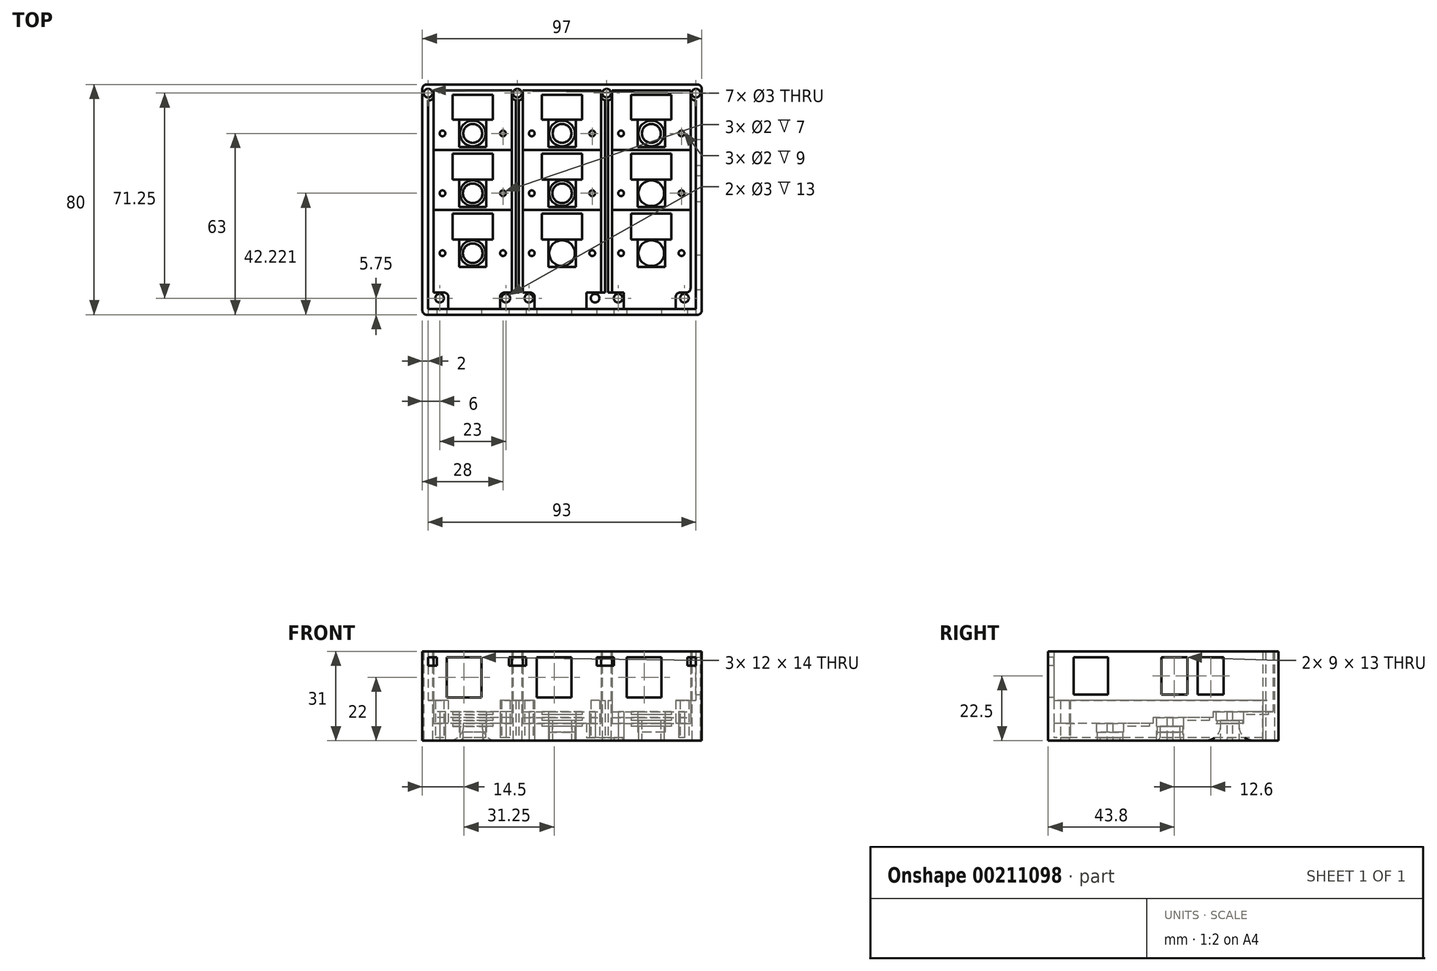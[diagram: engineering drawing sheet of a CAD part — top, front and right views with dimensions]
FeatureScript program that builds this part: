
annotation { "Feature Type Name" : "Feature", "Feature Type Description" : "" }
export const myFeature = defineFeature(function(context is Context, id is Id, definition is map)
    precondition{}
    {
        {
            var Q0;
            Q0=qCreatedBy(makeId("Top.planeOp"),FACE);
            var sketch = newSketch(context, id + "F0", { "sketchPlane" : qUnion([Q0])});
            skLineSegment(sketch, "E0.bottom", {"start": v(33, -40) * mm, "end": v(-33, -40) * mm});
            skLineSegment(sketch, "E0.top", {"start": v(33, 40) * mm, "end": v(-33, 40) * mm});
            skLineSegment(sketch, "E0.right", {"start": v(-33, -40) * mm, "end": v(-33, 40) * mm});
            skPoint(sketch, "E0.middle", {"position": v(0, 0) * mm});
            skLineSegment(sketch, "E1.bottom", {"start": v(31, -38) * mm, "end": v(-31, -38) * mm});
            skLineSegment(sketch, "E1.top", {"start": v(31, 38) * mm, "end": v(-31, 38) * mm});
            skLineSegment(sketch, "E1.right", {"start": v(-31, -38) * mm, "end": v(-31, 38) * mm});
            skLineSegment(sketch, "E2.bottom", {"start": v(-31, 38) * mm, "end": v(-28, 38) * mm});
            skLineSegment(sketch, "E2.left", {"start": v(-31, 38) * mm, "end": v(-31, 34.5) * mm});
            skLineSegment(sketch, "E3.bottom", {"start": v(-1.88, 38) * mm, "end": v(1.88, 38) * mm});
            skLineSegment(sketch, "E3.top", {"start": v(-1.88, 34.5) * mm, "end": v(1.88, 34.5) * mm});
            skLineSegment(sketch, "E3.left", {"start": v(-1.88, 38) * mm, "end": v(-1.88, 34.5) * mm});
            skLineSegment(sketch, "E3.right", {"start": v(1.88, 38) * mm, "end": v(1.88, 34.5) * mm});
            skLineSegment(sketch, "E4.MirrorCS", {"start": v(31, 38) * mm, "end": v(28, 38) * mm});
            skLineSegment(sketch, "E5", {"start": v(-31, -32.3) * mm, "end": v(33, -32.3) * mm});
            skCircle(sketch, "E6", {"center": v(-27, -34.25) * mm, "radius": 1.5 * mm});
            skCircle(sketch, "E7", {"center": v(-4, -34.25) * mm, "radius": 1.5 * mm});
            skCircle(sketch, "E8.MirrorC", {"center": v(4, -34.25) * mm, "radius": 1.5 * mm});
            skCircle(sketch, "E9.MirrorC", {"center": v(27, -34.25) * mm, "radius": 1.5 * mm});
            skLineSegment(sketch, "E10", {"start": v(-1.88, 34.5) * mm, "end": v(-1.88, -32.3) * mm});
            skLineSegment(sketch, "E11.MirrorCS", {"start": v(1.88, 34.5) * mm, "end": v(1.88, -32.3) * mm});
            skPoint(sketch, "E12.centerSnap0", {"position": v(0, 34.5) * mm});
            skCircle(sketch, "E13", {"center": v(-15.5, 23) * mm, "radius": 4.45 * mm});
            skCircle(sketch, "E14", {"center": v(-15.5, 23) * mm, "radius": 3.28 * mm});
            skLineSegment(sketch, "E15.bottom", {"start": v(-10.75, 18.25) * mm, "end": v(-20.25, 18.25) * mm});
            skLineSegment(sketch, "E15.top", {"start": v(-10.75, 27.75) * mm, "end": v(-20.25, 27.75) * mm});
            skLineSegment(sketch, "E15.left", {"start": v(-10.75, 18.25) * mm, "end": v(-10.75, 27.75) * mm});
            skLineSegment(sketch, "E15.right", {"start": v(-20.25, 18.25) * mm, "end": v(-20.25, 27.75) * mm});
            skLineSegment(sketch, "E16.bottom", {"start": v(-22.5, 36.38) * mm, "end": v(-8.5, 36.38) * mm});
            skLineSegment(sketch, "E16.top", {"start": v(-22.5, 27.75) * mm, "end": v(-8.5, 27.75) * mm});
            skLineSegment(sketch, "E16.left", {"start": v(-22.5, 36.38) * mm, "end": v(-22.5, 27.75) * mm});
            skLineSegment(sketch, "E16.right", {"start": v(-8.5, 36.38) * mm, "end": v(-8.5, 27.75) * mm});
            skCircle(sketch, "E17", {"center": v(-15.5, 2.22) * mm, "radius": 4.45 * mm});
            skCircle(sketch, "E18", {"center": v(-15.5, 2.22) * mm, "radius": 3.4 * mm});
            skLineSegment(sketch, "E19.bottom", {"start": v(-10.75, -2.53) * mm, "end": v(-20.25, -2.53) * mm});
            skLineSegment(sketch, "E19.top", {"start": v(-10.75, 6.97) * mm, "end": v(-20.25, 6.97) * mm});
            skLineSegment(sketch, "E19.left", {"start": v(-10.75, -2.53) * mm, "end": v(-10.75, 6.97) * mm});
            skLineSegment(sketch, "E19.right", {"start": v(-20.25, -2.53) * mm, "end": v(-20.25, 6.97) * mm});
            skLineSegment(sketch, "E20.bottom", {"start": v(-22.5, 15.97) * mm, "end": v(-8.5, 15.97) * mm});
            skLineSegment(sketch, "E20.top", {"start": v(-22.5, 6.97) * mm, "end": v(-8.5, 6.97) * mm});
            skLineSegment(sketch, "E20.left", {"start": v(-22.5, 15.97) * mm, "end": v(-22.5, 6.97) * mm});
            skLineSegment(sketch, "E20.right", {"start": v(-8.5, 15.97) * mm, "end": v(-8.5, 6.97) * mm});
            skCircle(sketch, "E21", {"center": v(-15.5, -18.6) * mm, "radius": 4.45 * mm});
            skCircle(sketch, "E22", {"center": v(-15.5, -18.6) * mm, "radius": 3.4 * mm});
            skLineSegment(sketch, "E23.bottom", {"start": v(-10.75, -23.35) * mm, "end": v(-20.25, -23.35) * mm});
            skLineSegment(sketch, "E23.top", {"start": v(-10.75, -13.85) * mm, "end": v(-20.25, -13.85) * mm});
            skLineSegment(sketch, "E23.left", {"start": v(-10.75, -23.35) * mm, "end": v(-10.75, -13.85) * mm});
            skLineSegment(sketch, "E23.right", {"start": v(-20.25, -23.35) * mm, "end": v(-20.25, -13.85) * mm});
            skLineSegment(sketch, "E24.bottom", {"start": v(-22.5, -4.85) * mm, "end": v(-8.5, -4.85) * mm});
            skLineSegment(sketch, "E24.top", {"start": v(-22.5, -13.85) * mm, "end": v(-8.5, -13.85) * mm});
            skLineSegment(sketch, "E24.left", {"start": v(-22.5, -4.85) * mm, "end": v(-22.5, -13.85) * mm});
            skLineSegment(sketch, "E24.right", {"start": v(-8.5, -4.85) * mm, "end": v(-8.5, -13.85) * mm});
            skLineSegment(sketch, "E25.MirrorCS", {"start": v(8.5, 36.38) * mm, "end": v(8.5, 27.75) * mm});
            skLineSegment(sketch, "E26.MirrorCS", {"start": v(22.5, 36.38) * mm, "end": v(8.5, 36.38) * mm});
            skLineSegment(sketch, "E27.MirrorCS", {"start": v(22.5, 36.38) * mm, "end": v(22.5, 27.75) * mm});
            skLineSegment(sketch, "E28.MirrorCS", {"start": v(22.5, 27.75) * mm, "end": v(8.5, 27.75) * mm});
            skCircle(sketch, "E29.MirrorC", {"center": v(15.5, 23) * mm, "radius": 4.45 * mm});
            skCircle(sketch, "E30.MirrorC", {"center": v(15.5, 23) * mm, "radius": 3.28 * mm});
            skLineSegment(sketch, "E31.MirrorCS", {"start": v(22.5, 15.97) * mm, "end": v(8.5, 15.97) * mm});
            skLineSegment(sketch, "E32.MirrorCS", {"start": v(8.5, 15.97) * mm, "end": v(8.5, 6.97) * mm});
            skLineSegment(sketch, "E33.MirrorCS", {"start": v(10.75, 6.97) * mm, "end": v(20.25, 6.97) * mm});
            skLineSegment(sketch, "E34.MirrorCS", {"start": v(22.5, 6.97) * mm, "end": v(8.5, 6.97) * mm});
            skLineSegment(sketch, "E35.MirrorCS", {"start": v(22.5, 15.97) * mm, "end": v(22.5, 6.97) * mm});
            skCircle(sketch, "E36.MirrorC", {"center": v(15.5, 2.22) * mm, "radius": 3.4 * mm});
            skCircle(sketch, "E37.MirrorC", {"center": v(15.5, 2.22) * mm, "radius": 4.45 * mm});
            skLineSegment(sketch, "E38.MirrorCS", {"start": v(10.75, -2.53) * mm, "end": v(20.25, -2.53) * mm});
            skLineSegment(sketch, "E39.MirrorCS", {"start": v(10.75, -2.53) * mm, "end": v(10.75, 6.97) * mm});
            skLineSegment(sketch, "E40.MirrorCS", {"start": v(20.25, -2.53) * mm, "end": v(20.25, 6.97) * mm});
            skLineSegment(sketch, "E41.MirrorCS", {"start": v(10.75, 18.25) * mm, "end": v(10.75, 27.75) * mm});
            skLineSegment(sketch, "E42.MirrorCS", {"start": v(10.75, 18.25) * mm, "end": v(20.25, 18.25) * mm});
            skLineSegment(sketch, "E43.MirrorCS", {"start": v(20.25, 18.25) * mm, "end": v(20.25, 27.75) * mm});
            skLineSegment(sketch, "E44.MirrorCS", {"start": v(22.5, -4.85) * mm, "end": v(8.5, -4.85) * mm});
            skLineSegment(sketch, "E45.MirrorCS", {"start": v(8.5, -4.85) * mm, "end": v(8.5, -13.85) * mm});
            skLineSegment(sketch, "E46.MirrorCS", {"start": v(22.5, -4.85) * mm, "end": v(22.5, -13.85) * mm});
            skLineSegment(sketch, "E47.MirrorCS", {"start": v(10.75, -13.85) * mm, "end": v(20.25, -13.85) * mm});
            skLineSegment(sketch, "E48.MirrorCS", {"start": v(22.5, -13.85) * mm, "end": v(8.5, -13.85) * mm});
            skLineSegment(sketch, "E49.MirrorCS", {"start": v(20.25, -23.35) * mm, "end": v(20.25, -13.85) * mm});
            skCircle(sketch, "E50.MirrorC", {"center": v(15.5, -18.6) * mm, "radius": 4.45 * mm});
            skCircle(sketch, "E51.MirrorC", {"center": v(15.5, -18.6) * mm, "radius": 3.4 * mm});
            skLineSegment(sketch, "E52.MirrorCS", {"start": v(10.75, -23.35) * mm, "end": v(20.25, -23.35) * mm});
            skLineSegment(sketch, "E53.MirrorCS", {"start": v(10.75, -23.35) * mm, "end": v(10.75, -13.85) * mm});
            skLineSegment(sketch, "E54.bottom", {"start": v(-0.5, 34.5) * mm, "end": v(0.5, 34.5) * mm});
            skLineSegment(sketch, "E54.top", {"start": v(-0.5, -32.3) * mm, "end": v(0.5, -32.3) * mm});
            skLineSegment(sketch, "E54.left", {"start": v(-0.5, 34.5) * mm, "end": v(-0.5, -32.3) * mm});
            skLineSegment(sketch, "E54.right", {"start": v(0.5, 34.5) * mm, "end": v(0.5, -32.3) * mm});
            skCircle(sketch, "E55", {"center": v(-31, 37) * mm, "radius": 1.5 * mm});
            skCircle(sketch, "E56", {"center": v(0, 37) * mm, "radius": 1.5 * mm});
            skLineSegment(sketch, "E57", {"start": v(-24, -32.3) * mm, "end": v(-24, -38) * mm});
            skLineSegment(sketch, "E58", {"start": v(-6, -32.3) * mm, "end": v(-6, -38) * mm});
            skLineSegment(sketch, "E59.MirrorCS", {"start": v(6, -32.3) * mm, "end": v(6, -38) * mm});
            skLineSegment(sketch, "E60.MirrorCS", {"start": v(24, -32.3) * mm, "end": v(24, -38) * mm});
            skCircle(sketch, "E61", {"center": v(-5, -18.6) * mm, "radius": 1 * mm});
            skCircle(sketch, "E62", {"center": v(-5, 2.22) * mm, "radius": 1 * mm});
            skCircle(sketch, "E63", {"center": v(-5, 23) * mm, "radius": 1 * mm});
            skLineSegment(sketch, "E64", {"start": v(-15.5, 23) * mm, "end": v(-15.5, -18.6) * mm, "construction": true});
            skCircle(sketch, "E65.MirrorC", {"center": v(-26, 23) * mm, "radius": 1 * mm});
            skCircle(sketch, "E66.MirrorC", {"center": v(-26, 2.22) * mm, "radius": 1 * mm});
            skCircle(sketch, "E67.MirrorC", {"center": v(-26, -18.6) * mm, "radius": 1 * mm});
            skCircle(sketch, "E68.MirrorC", {"center": v(5, 23) * mm, "radius": 1 * mm});
            skCircle(sketch, "E69.MirrorC", {"center": v(5, 2.22) * mm, "radius": 1 * mm});
            skCircle(sketch, "E70.MirrorC", {"center": v(5, -18.6) * mm, "radius": 1 * mm});
            skCircle(sketch, "E71.MirrorC", {"center": v(26, -18.6) * mm, "radius": 1 * mm});
            skCircle(sketch, "E72.MirrorC", {"center": v(26, 2.22) * mm, "radius": 1 * mm});
            skCircle(sketch, "E73.MirrorC", {"center": v(26, 23) * mm, "radius": 1 * mm});
            skLineSegment(sketch, "E74", {"start": v(15.5, 23) * mm, "end": v(15.5, -55.98) * mm, "construction": true});
            skCircle(sketch, "E75.MirrorC", {"center": v(46.5, 23) * mm, "radius": 4.45 * mm});
            skCircle(sketch, "E76.MirrorC", {"center": v(46.5, 23) * mm, "radius": 3.28 * mm});
            skLineSegment(sketch, "E77.MirrorCS", {"start": v(41.75, 27.75) * mm, "end": v(51.25, 27.75) * mm});
            skLineSegment(sketch, "E78.MirrorCS", {"start": v(53.5, 36.38) * mm, "end": v(53.5, 27.75) * mm});
            skLineSegment(sketch, "E79.MirrorCS", {"start": v(53.5, 36.38) * mm, "end": v(39.5, 36.38) * mm});
            skLineSegment(sketch, "E80.MirrorCS", {"start": v(39.5, 36.38) * mm, "end": v(39.5, 27.75) * mm});
            skLineSegment(sketch, "E81.MirrorCS", {"start": v(41.75, 18.25) * mm, "end": v(41.75, 27.75) * mm});
            skLineSegment(sketch, "E82.MirrorCS", {"start": v(51.25, 18.25) * mm, "end": v(51.25, 27.75) * mm});
            skLineSegment(sketch, "E83.MirrorCS", {"start": v(53.5, 27.75) * mm, "end": v(39.5, 27.75) * mm});
            skLineSegment(sketch, "E84.MirrorCS", {"start": v(41.75, 18.25) * mm, "end": v(51.25, 18.25) * mm});
            skLineSegment(sketch, "E85.MirrorCS", {"start": v(62, -38) * mm, "end": v(62, 38) * mm});
            skLineSegment(sketch, "E86.MirrorCS", {"start": v(64, -40) * mm, "end": v(64, 40) * mm});
            skLineSegment(sketch, "E87.MirrorCS", {"start": v(62, 38) * mm, "end": v(62, 34.5) * mm});
            skCircle(sketch, "E88.MirrorC", {"center": v(62, 37) * mm, "radius": 1.5 * mm});
            skLineSegment(sketch, "E89.MirrorCS", {"start": v(-2, 40) * mm, "end": v(64, 40) * mm});
            skLineSegment(sketch, "E90.MirrorCS", {"start": v(0, 38) * mm, "end": v(62, 38) * mm});
            skLineSegment(sketch, "E91.MirrorCS", {"start": v(51.25, -2.53) * mm, "end": v(51.25, 6.97) * mm});
            skLineSegment(sketch, "E92.MirrorCS", {"start": v(41.75, -2.53) * mm, "end": v(51.25, -2.53) * mm});
            skCircle(sketch, "E93.MirrorC", {"center": v(46.5, 2.22) * mm, "radius": 4.45 * mm});
            skCircle(sketch, "E94.MirrorC", {"center": v(46.5, 2.22) * mm, "radius": 3.4 * mm});
            skLineSegment(sketch, "E95.MirrorCS", {"start": v(53.5, 6.97) * mm, "end": v(39.5, 6.97) * mm});
            skLineSegment(sketch, "E96.MirrorCS", {"start": v(53.5, 15.97) * mm, "end": v(53.5, 6.97) * mm});
            skLineSegment(sketch, "E97.MirrorCS", {"start": v(53.5, 15.97) * mm, "end": v(39.5, 15.97) * mm});
            skLineSegment(sketch, "E98.MirrorCS", {"start": v(39.5, 15.97) * mm, "end": v(39.5, 6.97) * mm});
            skLineSegment(sketch, "E99.MirrorCS", {"start": v(41.75, -2.53) * mm, "end": v(41.75, 6.97) * mm});
            skLineSegment(sketch, "E100.MirrorCS", {"start": v(53.5, -4.85) * mm, "end": v(53.5, -13.85) * mm});
            skLineSegment(sketch, "E101.MirrorCS", {"start": v(53.5, -4.85) * mm, "end": v(39.5, -4.85) * mm});
            skLineSegment(sketch, "E102.MirrorCS", {"start": v(53.5, -13.85) * mm, "end": v(39.5, -13.85) * mm});
            skLineSegment(sketch, "E103.MirrorCS", {"start": v(51.25, -23.35) * mm, "end": v(51.25, -13.85) * mm});
            skCircle(sketch, "E104.MirrorC", {"center": v(46.5, -18.6) * mm, "radius": 4.45 * mm});
            skCircle(sketch, "E105.MirrorC", {"center": v(46.5, -18.6) * mm, "radius": 3.4 * mm});
            skLineSegment(sketch, "E106.MirrorCS", {"start": v(41.75, -23.35) * mm, "end": v(51.25, -23.35) * mm});
            skLineSegment(sketch, "E107.MirrorCS", {"start": v(41.75, -23.35) * mm, "end": v(41.75, -13.85) * mm});
            skLineSegment(sketch, "E108.MirrorCS", {"start": v(39.5, -4.85) * mm, "end": v(39.5, -13.85) * mm});
            skLineSegment(sketch, "E109.MirrorCS", {"start": v(62, -32.3) * mm, "end": v(-2, -32.3) * mm});
            skCircle(sketch, "E110.MirrorC", {"center": v(35, -34.25) * mm, "radius": 1.5 * mm});
            skLineSegment(sketch, "E111.MirrorCS", {"start": v(37, -32.3) * mm, "end": v(37, -38) * mm});
            skLineSegment(sketch, "E112.MirrorCS", {"start": v(55, -32.3) * mm, "end": v(55, -38) * mm});
            skLineSegment(sketch, "E113.MirrorCS", {"start": v(0, -38) * mm, "end": v(62, -38) * mm});
            skLineSegment(sketch, "E114.MirrorCS", {"start": v(-2, -40) * mm, "end": v(64, -40) * mm});
            skCircle(sketch, "E115.MirrorC", {"center": v(58, -34.25) * mm, "radius": 1.5 * mm});
            skCircle(sketch, "E116.MirrorC", {"center": v(36, -18.6) * mm, "radius": 1 * mm});
            skCircle(sketch, "E117.MirrorC", {"center": v(36, 2.22) * mm, "radius": 1 * mm});
            skCircle(sketch, "E118.MirrorC", {"center": v(57, 2.22) * mm, "radius": 1 * mm});
            skCircle(sketch, "E119.MirrorC", {"center": v(57, -18.6) * mm, "radius": 1 * mm});
            skCircle(sketch, "E120.MirrorC", {"center": v(57, 23) * mm, "radius": 1 * mm});
            skCircle(sketch, "E121.MirrorC", {"center": v(36, 23) * mm, "radius": 1 * mm});
            skLineSegment(sketch, "E122.MirrorCS", {"start": v(29.12, 34.5) * mm, "end": v(29.12, -32.3) * mm});
            skLineSegment(sketch, "E123.MirrorCS", {"start": v(30.5, 34.5) * mm, "end": v(30.5, -32.3) * mm});
            skLineSegment(sketch, "E124.MirrorCS", {"start": v(31.5, 34.5) * mm, "end": v(31.5, -32.3) * mm});
            skLineSegment(sketch, "E125.MirrorCS", {"start": v(32.88, 34.5) * mm, "end": v(32.88, -32.3) * mm});
            skCircle(sketch, "E126.MirrorC", {"center": v(31, 37) * mm, "radius": 1.5 * mm});
            skLineSegment(sketch, "E127.MirrorCS", {"start": v(29.12, 38) * mm, "end": v(29.12, 34.5) * mm});
            skLineSegment(sketch, "E128.MirrorCS", {"start": v(32.88, 38) * mm, "end": v(32.88, 34.5) * mm});
            skLineSegment(sketch, "E129.MirrorCS", {"start": v(32.88, 34.5) * mm, "end": v(29.12, 34.5) * mm});
            skLineSegment(sketch, "E130", {"start": v(-29.12, 34.5) * mm, "end": v(-29.12, -32.3) * mm});
            skLineSegment(sketch, "E131", {"start": v(-1.88, 17.24) * mm, "end": v(-29.12, 17.2) * mm});
            skLineSegment(sketch, "E132", {"start": v(-1.88, -3.6) * mm, "end": v(-29.12, -3.6) * mm});
            skLineSegment(sketch, "E133.MirrorCS", {"start": v(1.88, -3.6) * mm, "end": v(29.12, -3.6) * mm});
            skLineSegment(sketch, "E134.MirrorCS", {"start": v(1.88, 17.24) * mm, "end": v(29.12, 17.2) * mm});
            skLineSegment(sketch, "E135.MirrorCS", {"start": v(60.12, 34.5) * mm, "end": v(60.12, -32.3) * mm});
            skLineSegment(sketch, "E136.MirrorCS", {"start": v(32.87, 17.24) * mm, "end": v(60.12, 17.2) * mm});
            skLineSegment(sketch, "E137.MirrorCS", {"start": v(32.88, -3.6) * mm, "end": v(60.12, -3.6) * mm});
            skLineSegment(sketch, "E138", {"start": v(-29.12, 34.5) * mm, "end": v(-29.12, 38) * mm});
            skLineSegment(sketch, "E139.MirrorCS", {"start": v(60.12, 34.5) * mm, "end": v(60.12, 38) * mm});
            skLineSegment(sketch, "E140", {"start": v(-31, 34.5) * mm, "end": v(-29.12, 34.5) * mm});
            skLineSegment(sketch, "E141.MirrorCS", {"start": v(62, 34.5) * mm, "end": v(60.12, 34.5) * mm});
            skSolve(sketch);
        }
        {
            var Q0;
            Q0=makeQuery(id+"F0.imprint","IMPRINT",FACE,{"disambiguationData":[TD([[makeQuery(id+"F0.imprint","IMPRINT",EDGE,{"derivedFrom":sQuery(id+"F0.wireOp",EDGE,"E21")}),1.0]])]});
            var Q1;
            Q1=makeQuery(id+"F0.imprint","IMPRINT",FACE,{"disambiguationData":[TD([[makeQuery(id+"F0.imprint","IMPRINT",EDGE,{"derivedFrom":sQuery(id+"F0.wireOp",EDGE,"E54.bottom")}),-1.0]])]});
            var Q2;
            Q2=makeQuery(id+"F0.imprint","IMPRINT",FACE,{"disambiguationData":[TD([[makeQuery(id+"F0.imprint","IMPRINT",EDGE,{"derivedFrom":sQuery(id+"F0.wireOp",EDGE,"E50.MirrorC")}),-1.0]])]});
            var Q3;
            Q3=makeQuery(id+"F0.imprint","IMPRINT",FACE,{"disambiguationData":[TD([[makeQuery(id+"F0.imprint","IMPRINT",EDGE,{"derivedFrom":sQuery(id+"F0.wireOp",EDGE,"E66.MirrorC")}),-1.0]])]});
            var Q4;
            Q4=makeQuery(id+"F0.imprint","IMPRINT",FACE,{"disambiguationData":[TD([[makeQuery(id+"F0.imprint","IMPRINT",EDGE,{"derivedFrom":sQuery(id+"F0.wireOp",EDGE,"E67.MirrorC")}),-1.0]])]});
            var Q5;
            Q5=makeQuery(id+"F0.imprint","IMPRINT",FACE,{"disambiguationData":[TD([[makeQuery(id+"F0.imprint","IMPRINT",EDGE,{"derivedFrom":sQuery(id+"F0.wireOp",EDGE,"E61")}),1.0]])]});
            var Q6;
            Q6=makeQuery(id+"F0.imprint","IMPRINT",FACE,{"disambiguationData":[TD([[makeQuery(id+"F0.imprint","IMPRINT",EDGE,{"derivedFrom":sQuery(id+"F0.wireOp",EDGE,"E62")}),1.0]])]});
            var Q7;
            Q7=makeQuery(id+"F0.imprint","IMPRINT",FACE,{"disambiguationData":[TD([[makeQuery(id+"F0.imprint","IMPRINT",EDGE,{"derivedFrom":sQuery(id+"F0.wireOp",EDGE,"E69.MirrorC")}),-1.0]])]});
            var Q8;
            Q8=makeQuery(id+"F0.imprint","IMPRINT",FACE,{"disambiguationData":[TD([[makeQuery(id+"F0.imprint","IMPRINT",EDGE,{"derivedFrom":sQuery(id+"F0.wireOp",EDGE,"E70.MirrorC")}),-1.0]])]});
            var Q9;
            Q9=makeQuery(id+"F0.imprint","IMPRINT",FACE,{"disambiguationData":[TD([[makeQuery(id+"F0.imprint","IMPRINT",EDGE,{"derivedFrom":sQuery(id+"F0.wireOp",EDGE,"E71.MirrorC")}),1.0]])]});
            var Q10;
            Q10=makeQuery(id+"F0.imprint","IMPRINT",FACE,{"disambiguationData":[TD([[makeQuery(id+"F0.imprint","IMPRINT",EDGE,{"derivedFrom":sQuery(id+"F0.wireOp",EDGE,"E72.MirrorC")}),1.0]])]});
            var Q11;
            Q11=makeQuery(id+"F0.imprint","IMPRINT",FACE,{"disambiguationData":[TD([[makeQuery(id+"F0.imprint","IMPRINT",EDGE,{"derivedFrom":sQuery(id+"F0.wireOp",EDGE,"E7")}),1.0]])]});
            var Q12;
            Q12=makeQuery(id+"F0.imprint","IMPRINT",FACE,{"disambiguationData":[TD([[makeQuery(id+"F0.imprint","IMPRINT",EDGE,{"derivedFrom":sQuery(id+"F0.wireOp",EDGE,"E6")}),1.0]])]});
            var Q13;
            Q13=makeQuery(id+"F0.imprint","IMPRINT",FACE,{"disambiguationData":[TD([[makeQuery(id+"F0.imprint","IMPRINT",EDGE,{"derivedFrom":sQuery(id+"F0.wireOp",EDGE,"E8.MirrorC")}),-1.0]])]});
            var Q14;
            Q14=makeQuery(id+"F0.imprint","IMPRINT",FACE,{"disambiguationData":[TD([[makeQuery(id+"F0.imprint","IMPRINT",EDGE,{"derivedFrom":sQuery(id+"F0.wireOp",EDGE,"E9.MirrorC")}),-1.0]])]});
            var Q15;
            Q15=makeQuery(id+"F0.imprint","IMPRINT",FACE,{"disambiguationData":[TD([[makeQuery(id+"F0.imprint","IMPRINT",EDGE,{"derivedFrom":sQuery(id+"F0.wireOp",EDGE,"E65.MirrorC")}),-1.0]])]});
            var Q16;
            Q16=makeQuery(id+"F0.imprint","IMPRINT",FACE,{"disambiguationData":[TD([[makeQuery(id+"F0.imprint","IMPRINT",EDGE,{"derivedFrom":sQuery(id+"F0.wireOp",EDGE,"E63")}),1.0]])]});
            var Q17;
            Q17=makeQuery(id+"F0.imprint","IMPRINT",FACE,{"disambiguationData":[TD([[makeQuery(id+"F0.imprint","IMPRINT",EDGE,{"derivedFrom":sQuery(id+"F0.wireOp",EDGE,"E68.MirrorC")}),-1.0]])]});
            var Q18;
            Q18=makeQuery(id+"F0.imprint","IMPRINT",FACE,{"disambiguationData":[TD([[makeQuery(id+"F0.imprint","IMPRINT",EDGE,{"derivedFrom":sQuery(id+"F0.wireOp",EDGE,"E73.MirrorC")}),1.0]])]});
            var Q19;
            {var subQ0=sQuery(id+"F0.wireOp",EDGE,"E2.left");var subQ1=sQuery(id+"F0.wireOp",EDGE,"E2.bottom");var subQ2=makeQuery(id+"F0.imprint","INTERSECT",VERTEX,{"derivedFrom":[subQ1,subQ0]});Q19=makeQuery(id+"F0.imprint","IMPRINT",FACE,{"disambiguationData":[TD([[makeQuery(id+"F0.imprint","IMPRINT",EDGE,{"disambiguationData":[TD([[subQ2,-1.0]])],"derivedFrom":subQ1}),-1.0]])]});}
            var Q20;
            {var subQ0=sQuery(id+"F0.wireOp",EDGE,"E56");var subQ1=sQuery(id+"F0.wireOp",EDGE,"E3.bottom");var subQ2=makeQuery(id+"F0.imprint","INTERSECT",VERTEX,{"disambiguationData":[OD(0.0)],"derivedFrom":[subQ1,subQ0]});Q20=makeQuery(id+"F0.imprint","IMPRINT",FACE,{"disambiguationData":[TD([[makeQuery(id+"F0.imprint","IMPRINT",EDGE,{"disambiguationData":[TD([[subQ2,-1.0]])],"derivedFrom":subQ1}),-1.0]])]});}
            var Q21;
            {var subQ0=sQuery(id+"F0.wireOp",EDGE,"4bbdbd1b-dbbd-4441-a1b6-6a8d8a8a4ed50.MirrorCS");var subQ1=sQuery(id+"F0.wireOp",EDGE,"E4.MirrorCS");var subQ2=makeQuery(id+"F0.imprint","INTERSECT",VERTEX,{"derivedFrom":[subQ1,subQ0]});Q21=makeQuery(id+"F0.imprint","IMPRINT",FACE,{"disambiguationData":[TD([[makeQuery(id+"F0.imprint","IMPRINT",EDGE,{"disambiguationData":[TD([[subQ2,-1.0]])],"derivedFrom":subQ1}),1.0]])]});}
            var Q22;
            {var subQ0=sQuery(id+"F0.wireOp",EDGE,"E56");var subQ1=sQuery(id+"F0.wireOp",EDGE,"E3.bottom");var subQ2=makeQuery(id+"F0.imprint","INTERSECT",VERTEX,{"disambiguationData":[OD(0.0)],"derivedFrom":[subQ1,subQ0]});Q22=makeQuery(id+"F0.imprint","IMPRINT",FACE,{"disambiguationData":[TD([[makeQuery(id+"F0.imprint","IMPRINT",EDGE,{"disambiguationData":[TD([[subQ2,-1.0]])],"derivedFrom":subQ1}),1.0]])]});}
            var Q23;
            {var subQ0=sQuery(id+"F0.wireOp",EDGE,"E2.left");var subQ1=sQuery(id+"F0.wireOp",EDGE,"E2.bottom");var subQ2=makeQuery(id+"F0.imprint","INTERSECT",VERTEX,{"derivedFrom":[subQ1,subQ0]});Q23=makeQuery(id+"F0.imprint","IMPRINT",FACE,{"disambiguationData":[TD([[makeQuery(id+"F0.imprint","IMPRINT",EDGE,{"disambiguationData":[TD([[subQ2,-1.0]])],"derivedFrom":subQ1}),1.0]])]});}
            var Q24;
            {var subQ0=sQuery(id+"F0.wireOp",EDGE,"4bbdbd1b-dbbd-4441-a1b6-6a8d8a8a4ed50.MirrorCS");var subQ1=sQuery(id+"F0.wireOp",EDGE,"E4.MirrorCS");var subQ2=makeQuery(id+"F0.imprint","INTERSECT",VERTEX,{"derivedFrom":[subQ1,subQ0]});Q24=makeQuery(id+"F0.imprint","IMPRINT",FACE,{"disambiguationData":[TD([[makeQuery(id+"F0.imprint","IMPRINT",EDGE,{"disambiguationData":[TD([[subQ2,-1.0]])],"derivedFrom":subQ1}),-1.0]])]});}
            var Q25;
            {var subQ1=sQuery(id+"F0.wireOp",EDGE,"a819e3f4-d4a0-4d81-bf29-772e7b22f40c0.MirrorCS");Q25=makeQuery(id+"F0.imprint","IMPRINT",FACE,{"disambiguationData":[TD([[makeQuery(id+"F0.imprint","IMPRINT",EDGE,{"derivedFrom":subQ1}),1.0]])]});}
            var Q26;
            Q26=makeQuery(id+"F0.imprint","IMPRINT",FACE,{"disambiguationData":[TD([[makeQuery(id+"F0.imprint","IMPRINT",EDGE,{"derivedFrom":sQuery(id+"F0.wireOp",EDGE,"E104.MirrorC")}),-1.0]])]});
            var Q27;
            Q27=makeQuery(id+"F0.imprint","IMPRINT",FACE,{"disambiguationData":[TD([[makeQuery(id+"F0.imprint","IMPRINT",EDGE,{"derivedFrom":sQuery(id+"F0.wireOp",EDGE,"E110.MirrorC")}),-1.0]])]});
            var Q28;
            Q28=makeQuery(id+"F0.imprint","IMPRINT",FACE,{"disambiguationData":[TD([[makeQuery(id+"F0.imprint","IMPRINT",EDGE,{"derivedFrom":sQuery(id+"F0.wireOp",EDGE,"E71.MirrorC")}),1.0]])]});
            var Q29;
            Q29=makeQuery(id+"F0.imprint","IMPRINT",FACE,{"disambiguationData":[TD([[makeQuery(id+"F0.imprint","IMPRINT",EDGE,{"derivedFrom":sQuery(id+"F0.wireOp",EDGE,"E115.MirrorC")}),-1.0]])]});
            var Q30;
            Q30=makeQuery(id+"F0.imprint","IMPRINT",FACE,{"disambiguationData":[TD([[makeQuery(id+"F0.imprint","IMPRINT",EDGE,{"derivedFrom":sQuery(id+"F0.wireOp",EDGE,"E119.MirrorC")}),1.0]])]});
            var Q31;
            Q31=makeQuery(id+"F0.imprint","IMPRINT",FACE,{"disambiguationData":[TD([[makeQuery(id+"F0.imprint","IMPRINT",EDGE,{"derivedFrom":sQuery(id+"F0.wireOp",EDGE,"E116.MirrorC")}),-1.0]])]});
            var Q32;
            Q32=makeQuery(id+"F0.imprint","IMPRINT",FACE,{"disambiguationData":[TD([[makeQuery(id+"F0.imprint","IMPRINT",EDGE,{"derivedFrom":sQuery(id+"F0.wireOp",EDGE,"E72.MirrorC")}),1.0]])]});
            var Q33;
            Q33=makeQuery(id+"F0.imprint","IMPRINT",FACE,{"disambiguationData":[TD([[makeQuery(id+"F0.imprint","IMPRINT",EDGE,{"derivedFrom":sQuery(id+"F0.wireOp",EDGE,"E117.MirrorC")}),-1.0]])]});
            var Q34;
            Q34=makeQuery(id+"F0.imprint","IMPRINT",FACE,{"disambiguationData":[TD([[makeQuery(id+"F0.imprint","IMPRINT",EDGE,{"derivedFrom":sQuery(id+"F0.wireOp",EDGE,"E121.MirrorC")}),-1.0]])]});
            var Q35;
            Q35=makeQuery(id+"F0.imprint","IMPRINT",FACE,{"disambiguationData":[TD([[makeQuery(id+"F0.imprint","IMPRINT",EDGE,{"derivedFrom":sQuery(id+"F0.wireOp",EDGE,"E120.MirrorC")}),1.0]])]});
            var Q36;
            {var subQ0=sQuery(id+"F0.wireOp",EDGE,"E90.MirrorCS");var subQ1=makeQuery(id+"F0.imprint","IMPRINT",VERTEX,{"derivedFrom":subQ0});Q36=makeQuery(id+"F0.imprint","IMPRINT",FACE,{"disambiguationData":[TD([[makeQuery(id+"F0.imprint","IMPRINT",EDGE,{"disambiguationData":[TD([[subQ1,1.0]])],"derivedFrom":subQ0}),-1.0]])]});}
            var Q37;
            {var subQ0=sQuery(id+"F0.wireOp",EDGE,"E90.MirrorCS");var subQ1=sQuery(id+"F0.wireOp",EDGE,"E87.MirrorCS");var subQ2=makeQuery(id+"F0.imprint","INTERSECT",VERTEX,{"derivedFrom":[subQ1,subQ0]});Q37=makeQuery(id+"F0.imprint","IMPRINT",FACE,{"disambiguationData":[TD([[makeQuery(id+"F0.imprint","IMPRINT",EDGE,{"disambiguationData":[TD([[subQ2,-1.0]])],"derivedFrom":subQ1}),-1.0]])]});}
            var Q38;
            {var subQ0=sQuery(id+"F0.wireOp",EDGE,"E90.MirrorCS");var subQ1=makeQuery(id+"F0.imprint","IMPRINT",VERTEX,{"derivedFrom":subQ0});Q38=makeQuery(id+"F0.imprint","IMPRINT",FACE,{"disambiguationData":[TD([[makeQuery(id+"F0.imprint","IMPRINT",EDGE,{"disambiguationData":[TD([[subQ1,1.0]])],"derivedFrom":subQ0}),1.0]])]});}
            var Q39;
            {var subQ0=sQuery(id+"F0.wireOp",EDGE,"E90.MirrorCS");var subQ1=sQuery(id+"F0.wireOp",EDGE,"E87.MirrorCS");var subQ2=makeQuery(id+"F0.imprint","INTERSECT",VERTEX,{"derivedFrom":[subQ1,subQ0]});Q39=makeQuery(id+"F0.imprint","IMPRINT",FACE,{"disambiguationData":[TD([[makeQuery(id+"F0.imprint","IMPRINT",EDGE,{"disambiguationData":[TD([[subQ2,-1.0]])],"derivedFrom":subQ1}),1.0]])]});}
            var Q40;
            Q40=makeQuery(id+"F0.imprint","IMPRINT",FACE,{"disambiguationData":[TD([[makeQuery(id+"F0.imprint","IMPRINT",EDGE,{"derivedFrom":sQuery(id+"F0.wireOp",EDGE,"E118.MirrorC")}),1.0]])]});
            var Q41;
            {var subQ0=sQuery(id+"F0.wireOp",EDGE,"1d7a142f-2401-46ea-bbda-0649d409a4330.MirrorCS");Q41=makeQuery(id+"F0.imprint","IMPRINT",FACE,{"disambiguationData":[TD([[makeQuery(id+"F0.imprint","IMPRINT",EDGE,{"derivedFrom":subQ0}),1.0]])]});}
            var Q42;
            {var subQ0=sQuery(id+"F0.wireOp",EDGE,"E123.MirrorCS");Q42=makeQuery(id+"F0.imprint","IMPRINT",FACE,{"disambiguationData":[TD([[makeQuery(id+"F0.imprint","IMPRINT",EDGE,{"derivedFrom":subQ0}),1.0]])]});}
            extrude(context, id + "F1", {"entities" : qUnion([Q0, Q1, Q2, Q3, Q4, Q5, Q6, Q7, Q8, Q9, Q10, Q11, Q12, Q13, Q14, Q15, Q16, Q17, Q18, Q19, Q20, Q21, Q22, Q23, Q24, Q25, Q26, Q27, Q28, Q29, Q30, Q31, Q32, Q33, Q34, Q35, Q36, Q37, Q38, Q39, Q40, Q41, Q42]), "depth" : 1 * mm});
        }
        {
            var Q0;
            Q0=makeQuery(id+"F0.imprint","IMPRINT",FACE,{"disambiguationData":[TD([[makeQuery(id+"F0.imprint","IMPRINT",EDGE,{"derivedFrom":sQuery(id+"F0.wireOp",EDGE,"E21")}),-1.0]])]});
            var Q1;
            {var subQ0=sQuery(id+"F0.wireOp",EDGE,"E49.MirrorCS");Q1=makeQuery(id+"F0.imprint","IMPRINT",FACE,{"disambiguationData":[TD([[makeQuery(id+"F0.imprint","IMPRINT",EDGE,{"derivedFrom":subQ0}),1.0]])]});}
            var Q2;
            Q2=makeQuery(id+"F0.imprint","IMPRINT",FACE,{"disambiguationData":[TD([[makeQuery(id+"F0.imprint","IMPRINT",EDGE,{"derivedFrom":sQuery(id+"F0.wireOp",EDGE,"E17")}),1.0]])]});
            var Q3;
            Q3=makeQuery(id+"F0.imprint","IMPRINT",FACE,{"disambiguationData":[TD([[makeQuery(id+"F0.imprint","IMPRINT",EDGE,{"derivedFrom":sQuery(id+"F0.wireOp",EDGE,"E36.MirrorC")}),1.0]])]});
            var Q4;
            {var subQ0=sQuery(id+"F0.wireOp",EDGE,"E103.MirrorCS");Q4=makeQuery(id+"F0.imprint","IMPRINT",FACE,{"disambiguationData":[TD([[makeQuery(id+"F0.imprint","IMPRINT",EDGE,{"derivedFrom":subQ0}),1.0]])]});}
            var Q5;
            Q5=makeQuery(id+"F0.imprint","IMPRINT",FACE,{"disambiguationData":[TD([[makeQuery(id+"F0.imprint","IMPRINT",EDGE,{"derivedFrom":sQuery(id+"F0.wireOp",EDGE,"E93.MirrorC")}),-1.0]])]});
            extrude(context, id + "F2", {"entities" : qUnion([Q0, Q1, Q2, Q3, Q4, Q5]), "operationType" : NewBodyOperationType.ADD, "depth" : 3 * mm});
        }
        {
            var Q0;
            Q0=makeQuery(id+"F0.imprint","IMPRINT",FACE,{"disambiguationData":[TD([[makeQuery(id+"F0.imprint","IMPRINT",EDGE,{"derivedFrom":sQuery(id+"F0.wireOp",EDGE,"E20.bottom")}),-1.0]])]});
            var Q1;
            Q1=makeQuery(id+"F0.imprint","IMPRINT",FACE,{"disambiguationData":[TD([[makeQuery(id+"F0.imprint","IMPRINT",EDGE,{"derivedFrom":sQuery(id+"F0.wireOp",EDGE,"E13")}),-1.0]])]});
            var Q2;
            Q2=makeQuery(id+"F0.imprint","IMPRINT",FACE,{"disambiguationData":[TD([[makeQuery(id+"F0.imprint","IMPRINT",EDGE,{"derivedFrom":sQuery(id+"F0.wireOp",EDGE,"E31.MirrorCS")}),1.0]])]});
            var Q3;
            Q3=makeQuery(id+"F0.imprint","IMPRINT",FACE,{"disambiguationData":[TD([[makeQuery(id+"F0.imprint","IMPRINT",EDGE,{"derivedFrom":sQuery(id+"F0.wireOp",EDGE,"E29.MirrorC")}),1.0]])]});
            var Q4;
            {var subQ0=sQuery(id+"F0.wireOp",EDGE,"E96.MirrorCS");Q4=makeQuery(id+"F0.imprint","IMPRINT",FACE,{"disambiguationData":[TD([[makeQuery(id+"F0.imprint","IMPRINT",EDGE,{"derivedFrom":subQ0}),-1.0]])]});}
            var Q5;
            Q5=makeQuery(id+"F0.imprint","IMPRINT",FACE,{"disambiguationData":[TD([[makeQuery(id+"F0.imprint","IMPRINT",EDGE,{"derivedFrom":sQuery(id+"F0.wireOp",EDGE,"E75.MirrorC")}),1.0]])]});
            extrude(context, id + "F3", {"entities" : qUnion([Q0, Q1, Q2, Q3, Q4, Q5]), "operationType" : NewBodyOperationType.ADD, "depth" : 7 * mm});
        }
        {
            var Q0;
            Q0=makeQuery(id+"F0.imprint","IMPRINT",FACE,{"disambiguationData":[TD([[makeQuery(id+"F0.imprint","IMPRINT",EDGE,{"derivedFrom":sQuery(id+"F0.wireOp",EDGE,"E19.bottom")}),1.0]])]});
            var Q1;
            Q1=makeQuery(id+"F0.imprint","IMPRINT",FACE,{"disambiguationData":[TD([[makeQuery(id+"F0.imprint","IMPRINT",EDGE,{"derivedFrom":sQuery(id+"F0.wireOp",EDGE,"E31.MirrorCS")}),-1.0]])]});
            var Q2;
            {var subQ5=sQuery(id+"F0.wireOp",EDGE,"E91.MirrorCS");Q2=makeQuery(id+"F0.imprint","IMPRINT",FACE,{"disambiguationData":[TD([[makeQuery(id+"F0.imprint","IMPRINT",EDGE,{"derivedFrom":subQ5}),-1.0]])]});}
            extrude(context, id + "F4", {"entities" : qUnion([Q0, Q1, Q2]), "operationType" : NewBodyOperationType.ADD, "depth" : 8 * mm});
        }
        {
            var Q0;
            Q0=makeQuery(id+"F0.imprint","IMPRINT",FACE,{"disambiguationData":[TD([[makeQuery(id+"F0.imprint","IMPRINT",EDGE,{"derivedFrom":sQuery(id+"F0.wireOp",EDGE,"E16.bottom")}),-1.0]])]});
            var Q1;
            {var subQ3=sQuery(id+"F0.wireOp",EDGE,"E25.MirrorCS");Q1=makeQuery(id+"F0.imprint","IMPRINT",FACE,{"disambiguationData":[TD([[makeQuery(id+"F0.imprint","IMPRINT",EDGE,{"derivedFrom":subQ3}),1.0]])]});}
            var Q2;
            {var subQ1=sQuery(id+"F0.wireOp",EDGE,"E78.MirrorCS");Q2=makeQuery(id+"F0.imprint","IMPRINT",FACE,{"disambiguationData":[TD([[makeQuery(id+"F0.imprint","IMPRINT",EDGE,{"derivedFrom":subQ1}),-1.0]])]});}
            extrude(context, id + "F5", {"entities" : qUnion([Q0, Q1, Q2]), "operationType" : NewBodyOperationType.ADD, "depth" : 9 * mm});
        }
        {
            var Q0;
            {var subQ4=sQuery(id+"F0.wireOp",EDGE,"E3.left");Q0=makeQuery(id+"F0.imprint","IMPRINT",FACE,{"disambiguationData":[TD([[makeQuery(id+"F0.imprint","IMPRINT",EDGE,{"derivedFrom":subQ4}),-1.0]])]});}
            var Q1;
            {var subQ9=sQuery(id+"F0.wireOp",EDGE,"E3.right");Q1=makeQuery(id+"F0.imprint","IMPRINT",FACE,{"disambiguationData":[TD([[makeQuery(id+"F0.imprint","IMPRINT",EDGE,{"derivedFrom":subQ9}),1.0]])]});}
            var Q2;
            {var subQ5=sQuery(id+"F0.wireOp",EDGE,"0ee36956-4347-4c33-b409-07fdfe6817680.MirrorCS");Q2=makeQuery(id+"F0.imprint","IMPRINT",FACE,{"disambiguationData":[TD([[makeQuery(id+"F0.imprint","IMPRINT",EDGE,{"derivedFrom":subQ5}),-1.0]])]});}
            var Q3;
            {var subQ6=sQuery(id+"F0.wireOp",EDGE,"E78.MirrorCS");Q3=makeQuery(id+"F0.imprint","IMPRINT",FACE,{"disambiguationData":[TD([[makeQuery(id+"F0.imprint","IMPRINT",EDGE,{"derivedFrom":subQ6}),1.0]])]});}
            extrude(context, id + "F6", {"entities" : qUnion([Q0, Q1, Q2, Q3]), "operationType" : NewBodyOperationType.ADD, "depth" : 10 * mm});
        }
        {
            var Q0;
            Q0=makeQuery(id+"F0.imprint","IMPRINT",FACE,{"disambiguationData":[TD([[makeQuery(id+"F0.imprint","IMPRINT",EDGE,{"derivedFrom":sQuery(id+"F0.wireOp",EDGE,"E24.bottom")}),-1.0]])]});
            var Q1;
            Q1=makeQuery(id+"F0.imprint","IMPRINT",FACE,{"disambiguationData":[TD([[makeQuery(id+"F0.imprint","IMPRINT",EDGE,{"derivedFrom":sQuery(id+"F0.wireOp",EDGE,"E44.MirrorCS")}),1.0]])]});
            var Q2;
            Q2=makeQuery(id+"F0.imprint","IMPRINT",FACE,{"disambiguationData":[TD([[makeQuery(id+"F0.imprint","IMPRINT",EDGE,{"derivedFrom":sQuery(id+"F0.wireOp",EDGE,"E17")}),-1.0]])]});
            var Q3;
            Q3=makeQuery(id+"F0.imprint","IMPRINT",FACE,{"disambiguationData":[TD([[makeQuery(id+"F0.imprint","IMPRINT",EDGE,{"derivedFrom":sQuery(id+"F0.wireOp",EDGE,"E37.MirrorC")}),1.0]])]});
            var Q4;
            {var subQ4=sQuery(id+"F0.wireOp",EDGE,"E100.MirrorCS");Q4=makeQuery(id+"F0.imprint","IMPRINT",FACE,{"disambiguationData":[TD([[makeQuery(id+"F0.imprint","IMPRINT",EDGE,{"derivedFrom":subQ4}),-1.0]])]});}
            var Q5;
            {var subQ1=sQuery(id+"F0.wireOp",EDGE,"E91.MirrorCS");Q5=makeQuery(id+"F0.imprint","IMPRINT",FACE,{"disambiguationData":[TD([[makeQuery(id+"F0.imprint","IMPRINT",EDGE,{"derivedFrom":subQ1}),1.0]])]});}
            extrude(context, id + "F7", {"entities" : qUnion([Q0, Q1, Q2, Q3, Q4, Q5]), "operationType" : NewBodyOperationType.ADD, "depth" : 5 * mm});
        }
        {
            var Q0;
            {var subQ10=sQuery(id+"F0.wireOp",EDGE,"as5H9wRG-vlFi-IaeT-bpy4-L7joDgvUDys8");Q0=makeQuery(id+"F0.imprint","IMPRINT",FACE,{"disambiguationData":[TD([[makeQuery(id+"F0.imprint","IMPRINT",EDGE,{"derivedFrom":subQ10}),1.0]])]});}
            var Q1;
            {var subQ10=sQuery(id+"F0.wireOp",EDGE,"efb54391-69b0-4f1c-9c84-c88345ef56250.MirrorCS");Q1=makeQuery(id+"F0.imprint","IMPRINT",FACE,{"disambiguationData":[TD([[makeQuery(id+"F0.imprint","IMPRINT",EDGE,{"derivedFrom":subQ10}),-1.0]])]});}
            var Q2;
            Q2=makeQuery(id+"F0.imprint","IMPRINT",FACE,{"disambiguationData":[TD([[makeQuery(id+"F0.imprint","IMPRINT",EDGE,{"derivedFrom":sQuery(id+"F0.wireOp",EDGE,"E13")}),1.0]])]});
            var Q3;
            Q3=makeQuery(id+"F0.imprint","IMPRINT",FACE,{"disambiguationData":[TD([[makeQuery(id+"F0.imprint","IMPRINT",EDGE,{"derivedFrom":sQuery(id+"F0.wireOp",EDGE,"E29.MirrorC")}),-1.0]])]});
            var Q4;
            {var subQ0=sQuery(id+"F0.wireOp",EDGE,"E57");Q4=makeQuery(id+"F0.imprint","IMPRINT",FACE,{"disambiguationData":[TD([[makeQuery(id+"F0.imprint","IMPRINT",EDGE,{"derivedFrom":subQ0}),1.0]])]});}
            var Q5;
            {var subQ0=sQuery(id+"F0.wireOp",EDGE,"E59.MirrorCS");Q5=makeQuery(id+"F0.imprint","IMPRINT",FACE,{"disambiguationData":[TD([[makeQuery(id+"F0.imprint","IMPRINT",EDGE,{"derivedFrom":subQ0}),1.0]])]});}
            var Q6;
            {var subQ0=sQuery(id+"F0.wireOp",EDGE,"E111.MirrorCS");Q6=makeQuery(id+"F0.imprint","IMPRINT",FACE,{"disambiguationData":[TD([[makeQuery(id+"F0.imprint","IMPRINT",EDGE,{"derivedFrom":subQ0}),1.0]])]});}
            var Q7;
            {var subQ8=sQuery(id+"F0.wireOp",EDGE,"a2697284-5f4f-4e30-b8e9-a0291027fc0e0.MirrorCS");Q7=makeQuery(id+"F0.imprint","IMPRINT",FACE,{"disambiguationData":[TD([[makeQuery(id+"F0.imprint","IMPRINT",EDGE,{"derivedFrom":subQ8}),-1.0]])]});}
            var Q8;
            Q8=makeQuery(id+"F0.imprint","IMPRINT",FACE,{"disambiguationData":[TD([[makeQuery(id+"F0.imprint","IMPRINT",EDGE,{"derivedFrom":sQuery(id+"F0.wireOp",EDGE,"E75.MirrorC")}),-1.0]])]});
            var Q9;
            Q9=makeQuery(id+"F0.imprint","IMPRINT",FACE,{"disambiguationData":[TD([[makeQuery(id+"F0.imprint","IMPRINT",EDGE,{"derivedFrom":sQuery(id+"F0.wireOp",EDGE,"E23.bottom")}),1.0]])]});
            var Q10;
            Q10=makeQuery(id+"F0.imprint","IMPRINT",FACE,{"disambiguationData":[TD([[makeQuery(id+"F0.imprint","IMPRINT",EDGE,{"derivedFrom":sQuery(id+"F0.wireOp",EDGE,"E44.MirrorCS")}),-1.0]])]});
            var Q11;
            {var subQ5=sQuery(id+"F0.wireOp",EDGE,"E100.MirrorCS");Q11=makeQuery(id+"F0.imprint","IMPRINT",FACE,{"disambiguationData":[TD([[makeQuery(id+"F0.imprint","IMPRINT",EDGE,{"derivedFrom":subQ5}),1.0]])]});}
            extrude(context, id + "F8", {"entities" : qUnion([Q0, Q1, Q2, Q3, Q4, Q5, Q6, Q7, Q8, Q9, Q10, Q11]), "operationType" : NewBodyOperationType.ADD, "depth" : 6 * mm});
        }
        {
            var Q0;
            {var subQ7=sQuery(id+"F0.wireOp",EDGE,"E54.left");Q0=makeQuery(id+"F0.imprint","IMPRINT",FACE,{"disambiguationData":[TD([[makeQuery(id+"F0.imprint","IMPRINT",EDGE,{"derivedFrom":subQ7}),-1.0]])]});}
            var Q1;
            {var subQ5=sQuery(id+"F0.wireOp",EDGE,"E54.right");Q1=makeQuery(id+"F0.imprint","IMPRINT",FACE,{"disambiguationData":[TD([[makeQuery(id+"F0.imprint","IMPRINT",EDGE,{"derivedFrom":subQ5}),1.0]])]});}
            var Q2;
            {var subQ5=sQuery(id+"F0.wireOp",EDGE,"E2.top");Q2=makeQuery(id+"F0.imprint","IMPRINT",FACE,{"disambiguationData":[TD([[makeQuery(id+"F0.imprint","IMPRINT",EDGE,{"derivedFrom":subQ5}),-1.0]])]});}
            var Q3;
            {var subQ1=sQuery(id+"F0.wireOp",EDGE,"ab46168d-af6e-42de-824f-0888a4270b770.MirrorCS");Q3=makeQuery(id+"F0.imprint","IMPRINT",FACE,{"disambiguationData":[TD([[makeQuery(id+"F0.imprint","IMPRINT",EDGE,{"derivedFrom":subQ1}),1.0]])]});}
            var Q4;
            Q4=makeQuery(id+"F0.imprint","IMPRINT",FACE,{"disambiguationData":[TD([[makeQuery(id+"F0.imprint","IMPRINT",EDGE,{"derivedFrom":sQuery(id+"F0.wireOp",EDGE,"E6")}),-1.0]])]});
            var Q5;
            Q5=makeQuery(id+"F0.imprint","IMPRINT",FACE,{"disambiguationData":[TD([[makeQuery(id+"F0.imprint","IMPRINT",EDGE,{"derivedFrom":sQuery(id+"F0.wireOp",EDGE,"E7")}),-1.0]])]});
            var Q6;
            Q6=makeQuery(id+"F0.imprint","IMPRINT",FACE,{"disambiguationData":[TD([[makeQuery(id+"F0.imprint","IMPRINT",EDGE,{"derivedFrom":sQuery(id+"F0.wireOp",EDGE,"E9.MirrorC")}),1.0]])]});
            var Q7;
            {var subQ7=sQuery(id+"F0.wireOp",EDGE,"39177a82-2316-4fb4-a93a-6d32d1cb23ba0.MirrorCS");Q7=makeQuery(id+"F0.imprint","IMPRINT",FACE,{"disambiguationData":[TD([[makeQuery(id+"F0.imprint","IMPRINT",EDGE,{"derivedFrom":subQ7}),1.0]])]});}
            var Q8;
            {var subQ0=sQuery(id+"F0.wireOp",EDGE,"a819e3f4-d4a0-4d81-bf29-772e7b22f40c0.MirrorCS");Q8=makeQuery(id+"F0.imprint","IMPRINT",FACE,{"disambiguationData":[TD([[makeQuery(id+"F0.imprint","IMPRINT",EDGE,{"derivedFrom":subQ0}),-1.0]])]});}
            var Q9;
            {var subQ0=sQuery(id+"F0.wireOp",EDGE,"cd15d214-6c87-4102-83e1-9705ae7459630.MirrorCS");Q9=makeQuery(id+"F0.imprint","IMPRINT",FACE,{"disambiguationData":[TD([[makeQuery(id+"F0.imprint","IMPRINT",EDGE,{"derivedFrom":subQ0}),1.0]])]});}
            var Q10;
            {var subQ0=sQuery(id+"F0.wireOp",EDGE,"E112.MirrorCS");Q10=makeQuery(id+"F0.imprint","IMPRINT",FACE,{"disambiguationData":[TD([[makeQuery(id+"F0.imprint","IMPRINT",EDGE,{"derivedFrom":subQ0}),1.0]])]});}
            var Q11;
            {var subQ3=sQuery(id+"F0.wireOp",EDGE,"b6e59eed-b5e8-4de3-8956-2fd325e44a850.MirrorCS");Q11=makeQuery(id+"F0.imprint","IMPRINT",FACE,{"disambiguationData":[TD([[makeQuery(id+"F0.imprint","IMPRINT",EDGE,{"derivedFrom":subQ3}),1.0]])]});}
            var Q12;
            {var subQ7=sQuery(id+"F0.wireOp",EDGE,"E123.MirrorCS");Q12=makeQuery(id+"F0.imprint","IMPRINT",FACE,{"disambiguationData":[TD([[makeQuery(id+"F0.imprint","IMPRINT",EDGE,{"derivedFrom":subQ7}),-1.0]])]});}
            var Q13;
            {var subQ5=sQuery(id+"F0.wireOp",EDGE,"E124.MirrorCS");Q13=makeQuery(id+"F0.imprint","IMPRINT",FACE,{"disambiguationData":[TD([[makeQuery(id+"F0.imprint","IMPRINT",EDGE,{"derivedFrom":subQ5}),1.0]])]});}
            var Q14;
            {var subQ3=sQuery(id+"F0.wireOp",EDGE,"E141.MirrorCS");Q14=makeQuery(id+"F0.imprint","IMPRINT",FACE,{"disambiguationData":[TD([[makeQuery(id+"F0.imprint","IMPRINT",EDGE,{"derivedFrom":subQ3}),1.0]])]});}
            var Q15;
            {var subQ0=sQuery(id+"F0.wireOp",EDGE,"E140");Q15=makeQuery(id+"F0.imprint","IMPRINT",FACE,{"disambiguationData":[TD([[makeQuery(id+"F0.imprint","IMPRINT",EDGE,{"derivedFrom":subQ0}),-1.0]])]});}
            extrude(context, id + "F9", {"entities" : qUnion([Q0, Q1, Q2, Q3, Q4, Q5, Q6, Q7, Q8, Q9, Q10, Q11, Q12, Q13, Q14, Q15]), "operationType" : NewBodyOperationType.ADD, "depth" : 14 * mm});
        }
        {
            var Q0;
            {var subQ40=sQuery(id+"F0.wireOp",EDGE,"E0.bottom");Q0=makeQuery(id+"F0.imprint","IMPRINT",FACE,{"disambiguationData":[TD([[makeQuery(id+"F0.imprint","IMPRINT",EDGE,{"derivedFrom":subQ40}),-1.0]])]});}
            var Q1;
            {var subQ2=sQuery(id+"F0.wireOp",EDGE,"E2.top");Q1=makeQuery(id+"F0.imprint","IMPRINT",FACE,{"disambiguationData":[TD([[makeQuery(id+"F0.imprint","IMPRINT",EDGE,{"derivedFrom":subQ2}),1.0]])]});}
            var Q2;
            {var subQ0=sQuery(id+"F0.wireOp",EDGE,"E3.left");Q2=makeQuery(id+"F0.imprint","IMPRINT",FACE,{"disambiguationData":[TD([[makeQuery(id+"F0.imprint","IMPRINT",EDGE,{"derivedFrom":subQ0}),1.0]])]});}
            var Q3;
            {var subQ5=sQuery(id+"F0.wireOp",EDGE,"b727cb25-b5a2-420d-b2cb-503f449eb2150.MirrorCS");Q3=makeQuery(id+"F0.imprint","IMPRINT",FACE,{"disambiguationData":[TD([[makeQuery(id+"F0.imprint","IMPRINT",EDGE,{"derivedFrom":subQ5}),1.0]])]});}
            var Q4;
            {var subQ1=sQuery(id+"F0.wireOp",EDGE,"9c96630b-d440-4ed3-86c2-870449db28cc0.MirrorCS");Q4=makeQuery(id+"F0.imprint","IMPRINT",FACE,{"disambiguationData":[TD([[makeQuery(id+"F0.imprint","IMPRINT",EDGE,{"derivedFrom":subQ1}),1.0]])]});}
            var Q5;
            {var subQ0=sQuery(id+"F0.wireOp",EDGE,"E127.MirrorCS");Q5=makeQuery(id+"F0.imprint","IMPRINT",FACE,{"disambiguationData":[TD([[makeQuery(id+"F0.imprint","IMPRINT",EDGE,{"derivedFrom":subQ0}),1.0]])]});}
            var Q6;
            {var subQ0=sQuery(id+"F0.wireOp",EDGE,"E139.MirrorCS");Q6=makeQuery(id+"F0.imprint","IMPRINT",FACE,{"disambiguationData":[TD([[makeQuery(id+"F0.imprint","IMPRINT",EDGE,{"derivedFrom":subQ0}),-1.0]])]});}
            var Q7;
            {var subQ0=sQuery(id+"F0.wireOp",EDGE,"E138");Q7=makeQuery(id+"F0.imprint","IMPRINT",FACE,{"disambiguationData":[TD([[makeQuery(id+"F0.imprint","IMPRINT",EDGE,{"derivedFrom":subQ0}),1.0]])]});}
            extrude(context, id + "F10", {"entities" : qUnion([Q0, Q1, Q2, Q3, Q4, Q5, Q6, Q7]), "operationType" : NewBodyOperationType.ADD, "depth" : 31 * mm});
        }
        {
            var Q0;
            Q0=makeQuery(id+"F10.opExtrude","SWEPT_EDGE",EDGE,{"disambiguationData":[OSD([sQuery(id+"F0.wireOp",EDGE,"E2.top"),sQuery(id+"F0.wireOp",EDGE,"E2.right"),sQuery(id+"F0.wireOp",EDGE,"LkVBRL40-ysjR-bma5-BsWp-XQaLOT4uVfW8")])]});
            var Q1;
            Q1=makeQuery(id+"F10.opExtrude","SWEPT_EDGE",EDGE,{"disambiguationData":[OSD([sQuery(id+"F0.wireOp",EDGE,"E3.top"),sQuery(id+"F0.wireOp",EDGE,"E3.left"),sQuery(id+"F0.wireOp",EDGE,"E10")])]});
            var Q2;
            Q2=makeQuery(id+"F10.opExtrude","SWEPT_EDGE",EDGE,{"disambiguationData":[OSD([sQuery(id+"F0.wireOp",EDGE,"E3.top"),sQuery(id+"F0.wireOp",EDGE,"E3.right"),sQuery(id+"F0.wireOp",EDGE,"E11.MirrorCS")])]});
            var Q3;
            Q3=makeQuery(id+"F10.opExtrude","SWEPT_EDGE",EDGE,{"disambiguationData":[OSD([sQuery(id+"F0.wireOp",EDGE,"b727cb25-b5a2-420d-b2cb-503f449eb2150.MirrorCS"),sQuery(id+"F0.wireOp",EDGE,"ab46168d-af6e-42de-824f-0888a4270b770.MirrorCS"),sQuery(id+"F0.wireOp",EDGE,"cbafa517-04c6-4995-84ae-35f9c04b9aa00.MirrorCS")])]});
            var Q4;
            Q4=makeQuery(id+"F10.opExtrude","SWEPT_EDGE",EDGE,{"disambiguationData":[OSD([sQuery(id+"F0.wireOp",EDGE,"E0.bottom"),sQuery(id+"F0.wireOp",EDGE,"E0.right")])]});
            var Q5;
            Q5=makeQuery(id+"F10.opExtrude","SWEPT_EDGE",EDGE,{"disambiguationData":[OSD([sQuery(id+"F0.wireOp",EDGE,"E0.bottom"),sQuery(id+"F0.wireOp",EDGE,"E0.left")])]});
            var Q6;
            Q6=makeQuery(id+"F10.opExtrude","SWEPT_EDGE",EDGE,{"disambiguationData":[OSD([sQuery(id+"F0.wireOp",EDGE,"E0.top"),sQuery(id+"F0.wireOp",EDGE,"E0.left")])]});
            var Q7;
            Q7=makeQuery(id+"F10.opExtrude","SWEPT_EDGE",EDGE,{"disambiguationData":[OSD([sQuery(id+"F0.wireOp",EDGE,"E0.top"),sQuery(id+"F0.wireOp",EDGE,"E0.right")])]});
            var Q8;
            Q8=makeQuery(id+"F2.opExtrude","CAP_EDGE",EDGE,{"disambiguationData":[OSD([sQuery(id+"F0.wireOp",EDGE,"E18")])],"isStart":true});
            var Q9;
            Q9=makeQuery(id+"F2.opExtrude","CAP_EDGE",EDGE,{"disambiguationData":[OSD([sQuery(id+"F0.wireOp",EDGE,"E36.MirrorC")])],"isStart":true});
            var Q10;
            Q10=makeQuery(id+"F10.opExtrude","SWEPT_EDGE",EDGE,{"disambiguationData":[OSD([sQuery(id+"F0.wireOp",EDGE,"5e448dcd-88b5-4402-87fc-d68ac9d143520.MirrorCS"),sQuery(id+"F0.wireOp",EDGE,"0130ff9e-c3ff-4318-9fcf-fbf70a09fa310.MirrorCS"),sQuery(id+"F0.wireOp",EDGE,"7499bec9-91ed-4883-8f7f-a680d632e1ce0.MirrorCS")])]});
            var Q11;
            Q11=makeQuery(id+"F10.opExtrude","SWEPT_EDGE",EDGE,{"disambiguationData":[OSD([sQuery(id+"F0.wireOp",EDGE,"e6a19c2e-5617-421a-af27-4249b2f430080.MirrorCS"),sQuery(id+"F0.wireOp",EDGE,"9c96630b-d440-4ed3-86c2-870449db28cc0.MirrorCS"),sQuery(id+"F0.wireOp",EDGE,"cd15d214-6c87-4102-83e1-9705ae7459630.MirrorCS")])]});
            var Q12;
            Q12=makeQuery(id+"F10.opExtrude","SWEPT_EDGE",EDGE,{"disambiguationData":[OSD([sQuery(id+"F0.wireOp",EDGE,"E86.MirrorCS"),sQuery(id+"F0.wireOp",EDGE,"E89.MirrorCS")])]});
            var Q13;
            Q13=makeQuery(id+"F10.opExtrude","SWEPT_EDGE",EDGE,{"disambiguationData":[OSD([sQuery(id+"F0.wireOp",EDGE,"E86.MirrorCS"),sQuery(id+"F0.wireOp",EDGE,"E114.MirrorCS")])]});
            var Q14;
            Q14=makeQuery(id+"F2.opExtrude","CAP_EDGE",EDGE,{"disambiguationData":[OSD([sQuery(id+"F0.wireOp",EDGE,"E94.MirrorC")])],"isStart":true});
            var Q15;
            Q15=makeQuery(id+"F10.opExtrude","SWEPT_EDGE",EDGE,{"disambiguationData":[OSD([sQuery(id+"F0.wireOp",EDGE,"E125.MirrorCS"),sQuery(id+"F0.wireOp",EDGE,"E128.MirrorCS"),sQuery(id+"F0.wireOp",EDGE,"E129.MirrorCS")])]});
            var Q16;
            Q16=makeQuery(id+"F10.opExtrude","SWEPT_EDGE",EDGE,{"disambiguationData":[OSD([sQuery(id+"F0.wireOp",EDGE,"E122.MirrorCS"),sQuery(id+"F0.wireOp",EDGE,"E127.MirrorCS"),sQuery(id+"F0.wireOp",EDGE,"E129.MirrorCS")])]});
            var Q17;
            Q17=makeQuery(id+"F10.opExtrude","SWEPT_EDGE",EDGE,{"disambiguationData":[OSD([sQuery(id+"F0.wireOp",EDGE,"E135.MirrorCS"),sQuery(id+"F0.wireOp",EDGE,"E139.MirrorCS"),sQuery(id+"F0.wireOp",EDGE,"E141.MirrorCS")])]});
            var Q18;
            Q18=makeQuery(id+"F10.opExtrude","SWEPT_EDGE",EDGE,{"disambiguationData":[OSD([sQuery(id+"F0.wireOp",EDGE,"E130"),sQuery(id+"F0.wireOp",EDGE,"E138"),sQuery(id+"F0.wireOp",EDGE,"E140")])]});
            var Q19;
            Q19=makeQuery(id+"F9.opExtrude","SWEPT_EDGE",EDGE,{"disambiguationData":[OSD([sQuery(id+"F0.wireOp",EDGE,"E59.MirrorCS"),sQuery(id+"F0.wireOp",EDGE,"E109.MirrorCS")])]});
            var Q20;
            Q20=makeQuery(id+"F9.opExtrude","SWEPT_EDGE",EDGE,{"disambiguationData":[OSD([sQuery(id+"F0.wireOp",EDGE,"E60.MirrorCS"),sQuery(id+"F0.wireOp",EDGE,"E109.MirrorCS")])]});
            var Q21;
            Q21=makeQuery(id+"F9.opExtrude","SWEPT_EDGE",EDGE,{"disambiguationData":[OSD([sQuery(id+"F0.wireOp",EDGE,"E109.MirrorCS"),sQuery(id+"F0.wireOp",EDGE,"E111.MirrorCS")])]});
            var Q22;
            Q22=makeQuery(id+"F9.opExtrude","SWEPT_EDGE",EDGE,{"disambiguationData":[OSD([sQuery(id+"F0.wireOp",EDGE,"E5"),sQuery(id+"F0.wireOp",EDGE,"E58")])]});
            var Q23;
            Q23=makeQuery(id+"F9.opExtrude","SWEPT_EDGE",EDGE,{"disambiguationData":[OSD([sQuery(id+"F0.wireOp",EDGE,"E5"),sQuery(id+"F0.wireOp",EDGE,"E57")])]});
            fillet(context, id + "F11", {"entities" : qUnion([Q0, Q1, Q2, Q3, Q4, Q5, Q6, Q7, Q8, Q9, Q10, Q11, Q12, Q13, Q14, Q15, Q16, Q17, Q18, Q19, Q20, Q21, Q22, Q23]), "radius" : 1.5 * mm, "tangentPropagation" : true, "allowEdgeOverflow" : false});
        }
        {
            var Q0;
            Q0=makeQuery(id+"F8.opExtrude","CAP_EDGE",EDGE,{"disambiguationData":[OSD([sQuery(id+"F0.wireOp",EDGE,"E14")])],"isStart":true});
            var Q1;
            Q1=makeQuery(id+"F8.opExtrude","CAP_EDGE",EDGE,{"disambiguationData":[OSD([sQuery(id+"F0.wireOp",EDGE,"E30.MirrorC")])],"isStart":true});
            var Q2;
            Q2=makeQuery(id+"F8.opExtrude","CAP_EDGE",EDGE,{"disambiguationData":[OSD([sQuery(id+"F0.wireOp",EDGE,"E76.MirrorC")])],"isStart":true});
            fillet(context, id + "F12", {"entities" : qUnion([Q0, Q1, Q2]), "radius" : 5 * mm, "tangentPropagation" : true, "allowEdgeOverflow" : false});
        }
        {
            var Q0;
            Q0=makeQuery(id+"F10.opExtrude","SWEPT_FACE",FACE,{"disambiguationData":[OSD([sQuery(id+"F0.wireOp",EDGE,"E0.bottom")])]});
            var sketch = newSketch(context, id + "F13", { "sketchPlane" : qUnion([Q0])});
            skLineSegment(sketch, "E142.bottom", {"start": v(-28, 29) * mm, "end": v(-31, 29) * mm});
            skLineSegment(sketch, "E142.top", {"start": v(-28, 26) * mm, "end": v(-31, 26) * mm});
            skLineSegment(sketch, "E142.left", {"start": v(-28, 29) * mm, "end": v(-28, 26) * mm});
            skLineSegment(sketch, "E142.right", {"start": v(-31, 29) * mm, "end": v(-31, 26) * mm});
            skLineSegment(sketch, "E143.bottom", {"start": v(-24.5, 29) * mm, "end": v(-12.5, 29) * mm});
            skLineSegment(sketch, "E143.top", {"start": v(-24.5, 15) * mm, "end": v(-12.5, 15) * mm});
            skLineSegment(sketch, "E143.left", {"start": v(-24.5, 29) * mm, "end": v(-24.5, 15) * mm});
            skLineSegment(sketch, "E143.right", {"start": v(-12.5, 29) * mm, "end": v(-12.5, 15) * mm});
            skLineSegment(sketch, "E144.bottom", {"start": v(6.75, 29) * mm, "end": v(18.75, 29) * mm});
            skLineSegment(sketch, "E144.top", {"start": v(6.75, 15) * mm, "end": v(18.75, 15) * mm});
            skLineSegment(sketch, "E144.left", {"start": v(6.75, 29) * mm, "end": v(6.75, 15) * mm});
            skLineSegment(sketch, "E144.right", {"start": v(18.75, 29) * mm, "end": v(18.75, 15) * mm});
            skLineSegment(sketch, "E145.bottom", {"start": v(3, 26) * mm, "end": v(-3, 26) * mm});
            skLineSegment(sketch, "E145.top", {"start": v(3, 29) * mm, "end": v(-3, 29) * mm});
            skLineSegment(sketch, "E145.left", {"start": v(3, 26) * mm, "end": v(3, 29) * mm});
            skLineSegment(sketch, "E145.right", {"start": v(-3, 26) * mm, "end": v(-3, 29) * mm});
            skPoint(sketch, "E145.middle", {"position": v(0, 27.5) * mm});
            skLineSegment(sketch, "E146.bottom", {"start": v(38, 29) * mm, "end": v(50, 29) * mm});
            skLineSegment(sketch, "E146.top", {"start": v(38, 15) * mm, "end": v(50, 15) * mm});
            skLineSegment(sketch, "E146.left", {"start": v(38, 29) * mm, "end": v(38, 15) * mm});
            skLineSegment(sketch, "E146.right", {"start": v(50, 29) * mm, "end": v(50, 15) * mm});
            skLineSegment(sketch, "E147.bottom", {"start": v(33.5, 26) * mm, "end": v(27.5, 26) * mm});
            skLineSegment(sketch, "E147.top", {"start": v(33.5, 29) * mm, "end": v(27.5, 29) * mm});
            skLineSegment(sketch, "E147.left", {"start": v(33.5, 26) * mm, "end": v(33.5, 29) * mm});
            skLineSegment(sketch, "E147.right", {"start": v(27.5, 26) * mm, "end": v(27.5, 29) * mm});
            skPoint(sketch, "E147.middle", {"position": v(30.5, 27.5) * mm});
            skPoint(sketch, "E147.middle.positionSnap0", {"position": v(3, 27.5) * mm});
            skPoint(sketch, "E147.centerSnap0", {"position": v(3, 27.5) * mm});
            skLineSegment(sketch, "E148.bottom", {"start": v(59, 29) * mm, "end": v(62, 29) * mm});
            skLineSegment(sketch, "E148.top", {"start": v(59, 26) * mm, "end": v(62, 26) * mm});
            skLineSegment(sketch, "E148.left", {"start": v(59, 29) * mm, "end": v(59, 26) * mm});
            skLineSegment(sketch, "E148.right", {"start": v(62, 29) * mm, "end": v(62, 26) * mm});
            skSolve(sketch);
        }
        {
            var Q0;
            Q0=makeQuery(id+"F13.imprint","IMPRINT",FACE,{"disambiguationData":[TD([[makeQuery(id+"F13.imprint","IMPRINT",EDGE,{"derivedFrom":sQuery(id+"F13.wireOp",EDGE,"E143.bottom")}),-1.0]])]});
            var Q1;
            Q1=makeQuery(id+"F13.imprint","IMPRINT",FACE,{"disambiguationData":[TD([[makeQuery(id+"F13.imprint","IMPRINT",EDGE,{"derivedFrom":sQuery(id+"F13.wireOp",EDGE,"E144.bottom")}),-1.0]])]});
            var Q2;
            Q2=makeQuery(id+"F13.imprint","IMPRINT",FACE,{"disambiguationData":[TD([[makeQuery(id+"F13.imprint","IMPRINT",EDGE,{"derivedFrom":sQuery(id+"F13.wireOp",EDGE,"E145.bottom")}),-1.0]])]});
            var Q3;
            Q3=makeQuery(id+"F13.imprint","IMPRINT",FACE,{"disambiguationData":[TD([[makeQuery(id+"F13.imprint","IMPRINT",EDGE,{"derivedFrom":sQuery(id+"F13.wireOp",EDGE,"E147.bottom")}),-1.0]])]});
            var Q4;
            Q4=makeQuery(id+"F13.imprint","IMPRINT",FACE,{"disambiguationData":[TD([[makeQuery(id+"F13.imprint","IMPRINT",EDGE,{"derivedFrom":sQuery(id+"F13.wireOp",EDGE,"E146.bottom")}),-1.0]])]});
            var Q5;
            {var subQ0=sQuery(id+"F13.wireOp",EDGE,"E142.left");Q5=makeQuery(id+"F13.imprint","IMPRINT",FACE,{"disambiguationData":[TD([[makeQuery(id+"F13.imprint","IMPRINT",EDGE,{"derivedFrom":subQ0}),-1.0]])]});}
            var Q6;
            {var subQ0=sQuery(id+"F13.wireOp",EDGE,"E148.left");Q6=makeQuery(id+"F13.imprint","IMPRINT",FACE,{"disambiguationData":[TD([[makeQuery(id+"F13.imprint","IMPRINT",EDGE,{"derivedFrom":subQ0}),1.0]])]});}
            extrude(context, id + "F14", {"entities" : qUnion([Q0, Q1, Q2, Q3, Q4, Q5, Q6]), "operationType" : NewBodyOperationType.REMOVE, "endBound" : BoundingType.UP_TO_NEXT, "oppositeDirection" : true, "depth" : 25 * mm});
        }
        {
            var Q0;
            Q0=makeQuery(id+"F10.opExtrude","SWEPT_FACE",FACE,{"disambiguationData":[OSD([sQuery(id+"F0.wireOp",EDGE,"E86.MirrorCS")])]});
            var sketch = newSketch(context, id + "F15", { "sketchPlane" : qUnion([Q0])});
            skLineSegment(sketch, "E149.bottom", {"start": v(-19.2, 16) * mm, "end": v(-31.2, 16) * mm});
            skLineSegment(sketch, "E149.top", {"start": v(-19.2, 29) * mm, "end": v(-31.2, 29) * mm});
            skLineSegment(sketch, "E149.left", {"start": v(-19.2, 16) * mm, "end": v(-19.2, 29) * mm});
            skLineSegment(sketch, "E149.right", {"start": v(-31.2, 16) * mm, "end": v(-31.2, 29) * mm});
            skPoint(sketch, "E149.middle", {"position": v(-25.2, 22.5) * mm});
            skLineSegment(sketch, "E150.bottom", {"start": v(8.3, 16) * mm, "end": v(-0.7, 16) * mm});
            skLineSegment(sketch, "E150.top", {"start": v(8.3, 29) * mm, "end": v(-0.7, 29) * mm});
            skLineSegment(sketch, "E150.left", {"start": v(8.3, 16) * mm, "end": v(8.3, 29) * mm});
            skLineSegment(sketch, "E150.right", {"start": v(-0.7, 16) * mm, "end": v(-0.7, 29) * mm});
            skPoint(sketch, "E150.middle", {"position": v(3.8, 22.5) * mm});
            skPoint(sketch, "E150.cornerSnap0", {"position": v(-25.2, 16) * mm});
            skLineSegment(sketch, "E151.bottom", {"start": v(20.9, 16) * mm, "end": v(11.9, 16) * mm});
            skLineSegment(sketch, "E151.top", {"start": v(20.9, 29) * mm, "end": v(11.9, 29) * mm});
            skLineSegment(sketch, "E151.left", {"start": v(20.9, 16) * mm, "end": v(20.9, 29) * mm});
            skLineSegment(sketch, "E151.right", {"start": v(11.9, 16) * mm, "end": v(11.9, 29) * mm});
            skPoint(sketch, "E151.middle", {"position": v(16.4, 22.5) * mm});
            skSolve(sketch);
        }
        {
            var Q0;
            Q0=makeQuery(id+"F15.imprint","IMPRINT",FACE,{"disambiguationData":[TD([[makeQuery(id+"F15.imprint","IMPRINT",EDGE,{"derivedFrom":sQuery(id+"F15.wireOp",EDGE,"E149.bottom")}),-1.0]])]});
            var Q1;
            Q1=makeQuery(id+"F15.imprint","IMPRINT",FACE,{"disambiguationData":[TD([[makeQuery(id+"F15.imprint","IMPRINT",EDGE,{"derivedFrom":sQuery(id+"F15.wireOp",EDGE,"E150.bottom")}),-1.0]])]});
            var Q2;
            Q2=makeQuery(id+"F15.imprint","IMPRINT",FACE,{"disambiguationData":[TD([[makeQuery(id+"F15.imprint","IMPRINT",EDGE,{"derivedFrom":sQuery(id+"F15.wireOp",EDGE,"E151.bottom")}),-1.0]])]});
            extrude(context, id + "F16", {"entities" : qUnion([Q0, Q1, Q2]), "operationType" : NewBodyOperationType.REMOVE, "endBound" : BoundingType.UP_TO_NEXT, "oppositeDirection" : true, "depth" : 25 * mm});
        }
    });
